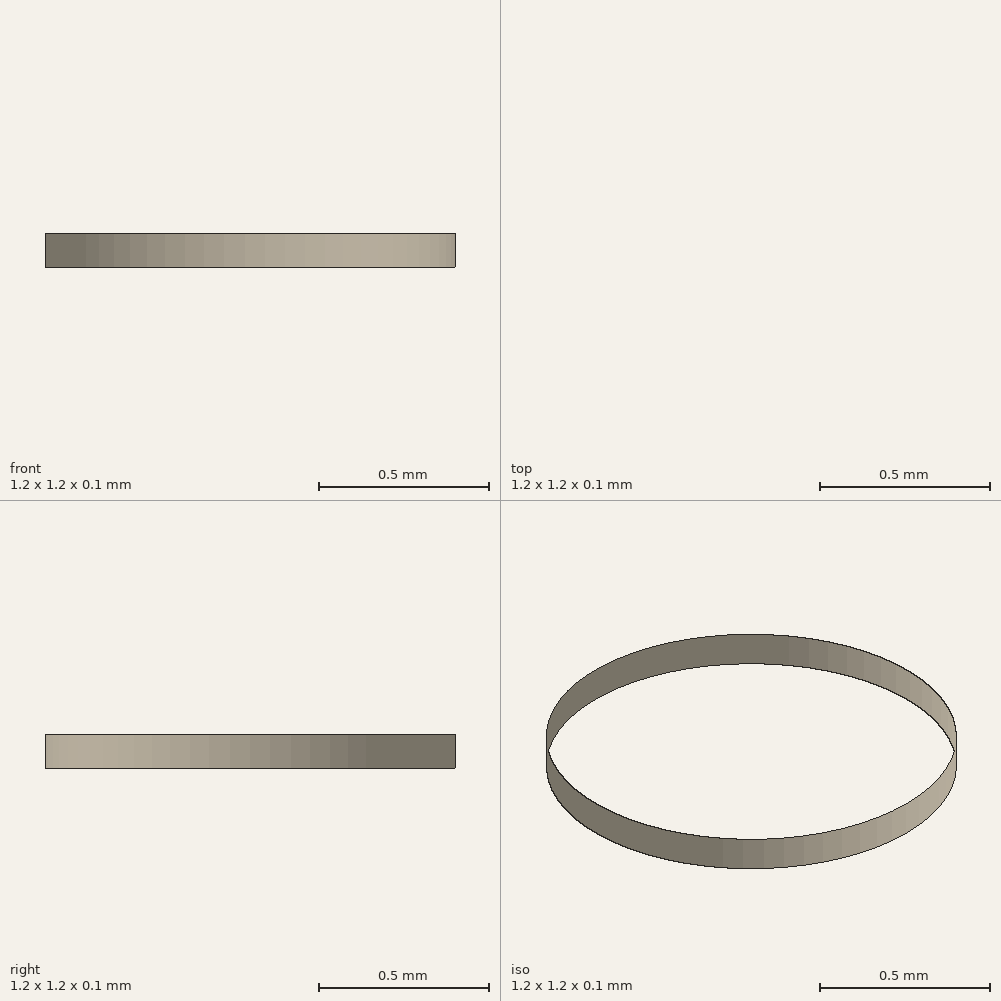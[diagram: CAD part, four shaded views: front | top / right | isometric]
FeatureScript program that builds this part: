
annotation { "Feature Type Name" : "Feature", "Feature Type Description" : "" }
export const myFeature = defineFeature(function(context is Context, id is Id, definition is map)
    precondition{}
    {
        {
            var Q0;
            Q0=qCreatedBy(makeId("Top.planeOp"),FACE);
            var sketch = newSketch(context, id + "F0", { "sketchPlane" : qUnion([Q0])});
            skCircle(sketch, "E0", {"center": v(0, 0) * mm, "radius": 0.6 * mm});
            skSolve(sketch);
        }
        {
            var Q0;
            Q0=sQuery(id+"F0.wireOp",EDGE,"E0");
            extrude(context, id + "F1", {"bodyType" : ToolBodyType.SURFACE, "surfaceEntities" : qUnion([Q0]), "depth" : 0.1 * mm});
        }
    });
